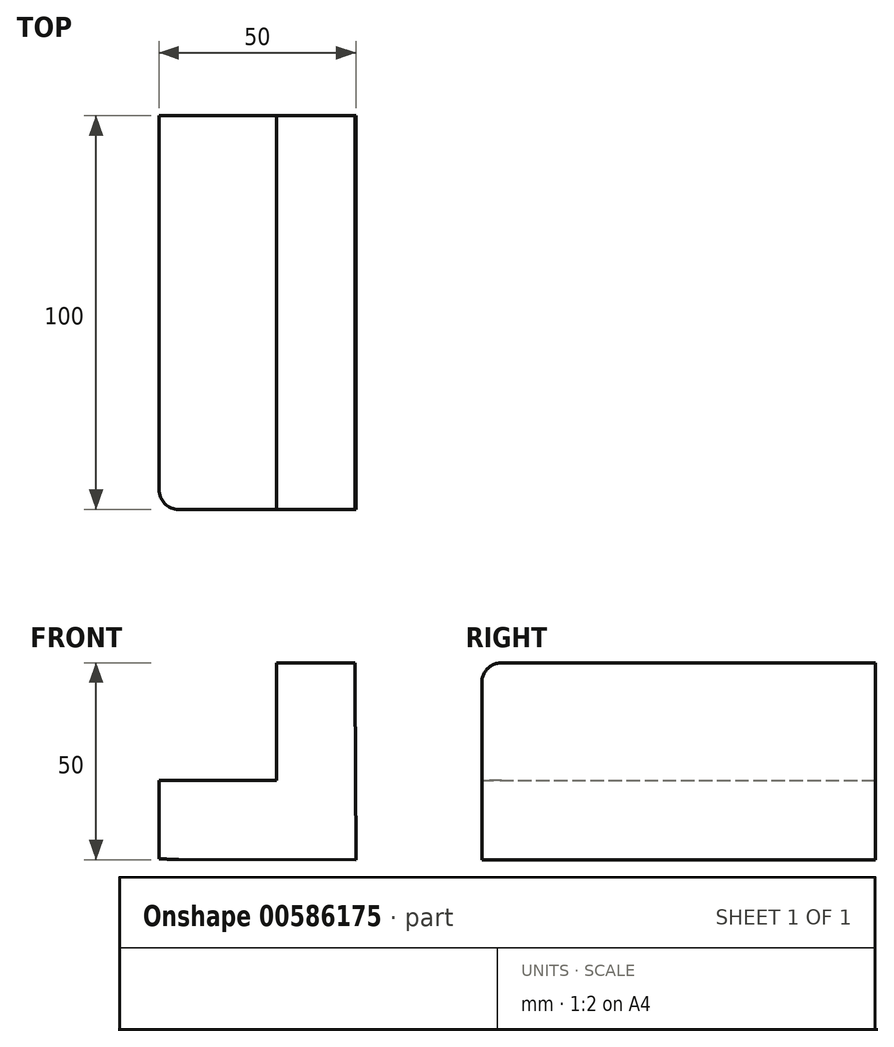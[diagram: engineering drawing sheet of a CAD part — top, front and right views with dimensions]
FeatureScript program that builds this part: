
annotation { "Feature Type Name" : "Feature", "Feature Type Description" : "" }
export const myFeature = defineFeature(function(context is Context, id is Id, definition is map)
    precondition{}
    {
        {
            var Q0;
            Q0=qCreatedBy(makeId("Front.planeOp"),FACE);
            var sketch = newSketch(context, id + "F0", { "sketchPlane" : qUnion([Q0])});
            skPoint(sketch, "E0.middle", {"position": v(0, 0) * mm});
            skLineSegment(sketch, "E1", {"start": v(0, 0) * mm, "end": v(0, 29.85) * mm});
            skLineSegment(sketch, "E2", {"start": v(0, 29.85) * mm, "end": v(20, 29.85) * mm});
            skLineSegment(sketch, "E3", {"start": v(20, 29.85) * mm, "end": v(20.17, -20.15) * mm});
            skLineSegment(sketch, "E4", {"start": v(20.17, -20.15) * mm, "end": v(-29.83, -20) * mm});
            skLineSegment(sketch, "E5", {"start": v(-29.83, -20) * mm, "end": v(-29.83, 0) * mm});
            skLineSegment(sketch, "E6", {"start": v(-29.83, 0) * mm, "end": v(0, 0) * mm});
            skSolve(sketch);
        }
        {
            var Q0;
            Q0 = qSketchRegion(id + "F0", true);
            extrude(context, id + "F1", {"entities" : qUnion([Q0]), "depth" : 100 * mm, "offsetDistance" : 25 * mm});
        }
        {
            var Q0;
            Q0=makeQuery(id+"F1.opExtrude","CAP_EDGE",EDGE,{"disambiguationData":[OSD([sQuery(id+"F0.wireOp",EDGE,"E2")])],"isStart":false});
            fillet(context, id + "F2", {"entities" : qUnion([Q0]), "radius" : 5 * mm, "tangentPropagation" : true, "allowEdgeOverflow" : false});
        }
        {
            var Q0;
            Q0=makeQuery(id+"F1.opExtrude","CAP_EDGE",EDGE,{"disambiguationData":[OSD([sQuery(id+"F0.wireOp",EDGE,"E5")])],"isStart":false});
            fillet(context, id + "F3", {"entities" : qUnion([Q0]), "radius" : 5 * mm, "tangentPropagation" : true, "allowEdgeOverflow" : false});
        }
    });
